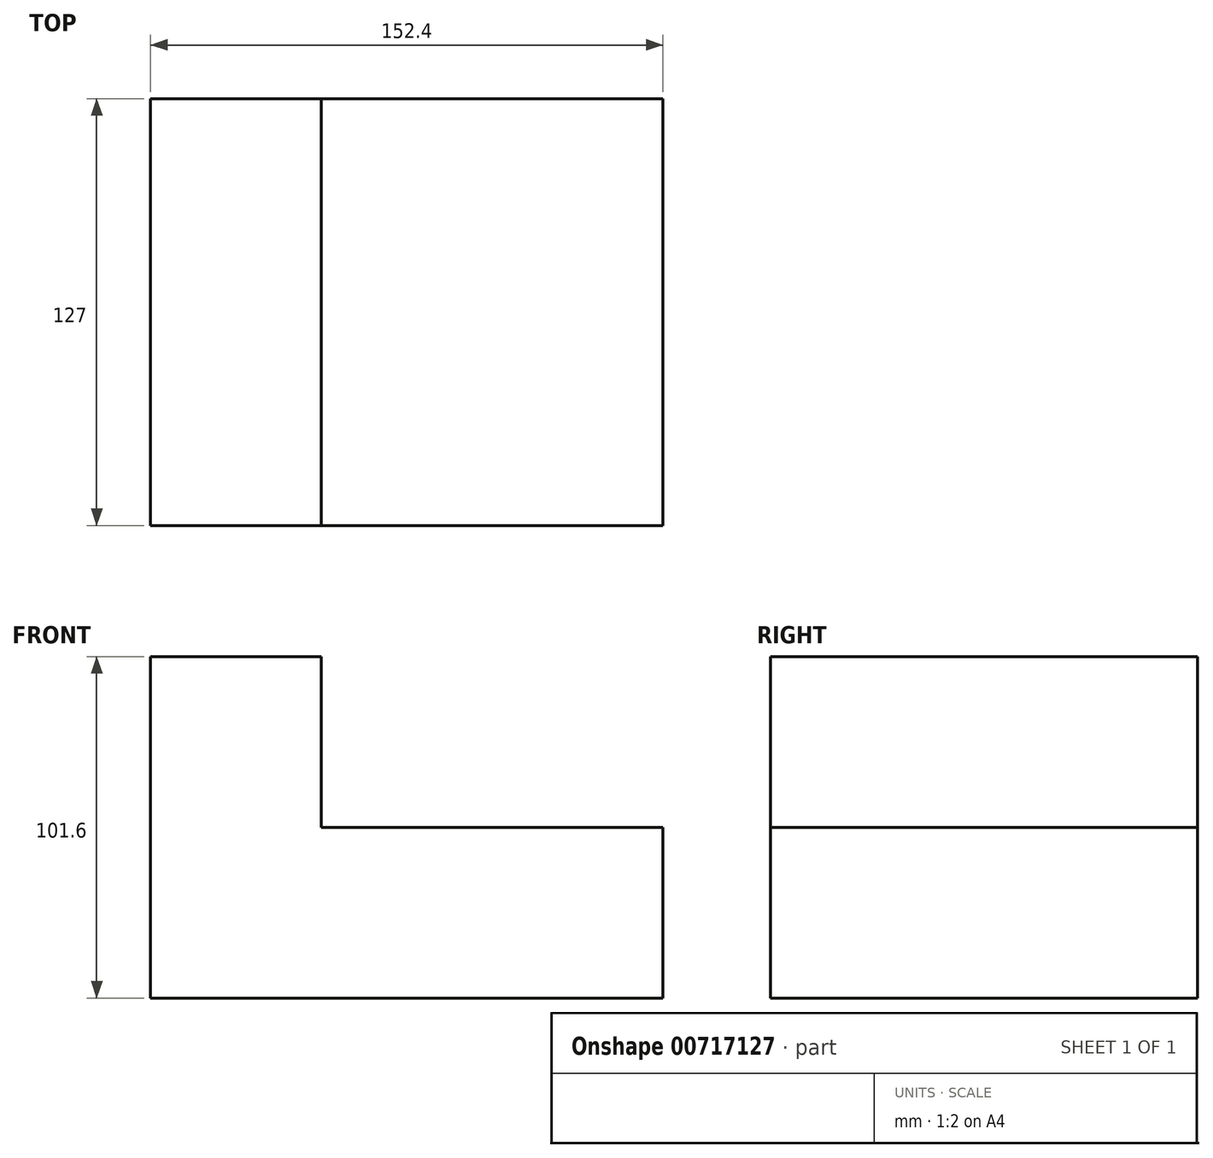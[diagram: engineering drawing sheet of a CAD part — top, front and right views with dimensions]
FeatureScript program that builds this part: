
annotation { "Feature Type Name" : "Feature", "Feature Type Description" : "" }
export const myFeature = defineFeature(function(context is Context, id is Id, definition is map)
    precondition{}
    {
        {
            var Q0;
            Q0=qCreatedBy(makeId("Front.planeOp"),FACE);
            var sketch = newSketch(context, id + "F0", { "sketchPlane" : qUnion([Q0])});
            skLineSegment(sketch, "E0", {"start": v(-82.6, -46.88) * mm, "end": v(69.8, -46.88) * mm});
            skLineSegment(sketch, "E1", {"start": v(-82.6, -46.88) * mm, "end": v(-82.6, 54.72) * mm});
            skLineSegment(sketch, "E2", {"start": v(-82.6, 54.72) * mm, "end": v(-31.8, 54.72) * mm});
            skLineSegment(sketch, "E3", {"start": v(-31.8, 54.72) * mm, "end": v(-31.8, 3.92) * mm});
            skLineSegment(sketch, "E4", {"start": v(-31.8, 3.92) * mm, "end": v(69.8, 3.92) * mm});
            skLineSegment(sketch, "E5", {"start": v(69.8, 3.92) * mm, "end": v(69.8, -46.88) * mm});
            skSolve(sketch);
        }
        {
            var Q0;
            Q0=makeQuery(id+"F0.imprint","IMPRINT",FACE,{"disambiguationData":[TD([[makeQuery(id+"F0.imprint","IMPRINT",EDGE,{"derivedFrom":sQuery(id+"F0.wireOp",EDGE,"E0")}),1.0]])]});
            extrude(context, id + "F1", {"entities" : qUnion([Q0]), "depth" : 127 * mm, "offsetDistance" : 25.4 * mm});
        }
    });
